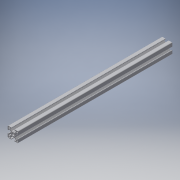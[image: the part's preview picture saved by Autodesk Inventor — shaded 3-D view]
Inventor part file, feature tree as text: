
AUTODESK INVENTOR PART (.ipt)
format: ipt  version: 2016 (Build 200138000, 138)  size: 312,832 bytes
history: native  units: in
note: dims shown in document units (in); Inventor stores cm internally (conversion verified against a paired STEP export)
features: other x3, extrude x1, sketch x1
ambient origin geometry x8: Origin, YZ Plane, XZ Plane, XY Plane, X Axis, Y Axis, Z Axis, Center Point
bodies: Solid1 (feature_tree)
feature tree (5):
  other  "Blocks"
  extrude  "Extrusion1"  [1 undecoded]
  sketch  "Sketch1"  dims[d1=0.0in]
  other  "Bosch 30x30 profile"
  other  "Bosch 30x30 profile:1"
note: 1 required parameter value undecoded (feature->parameter linkage not recoverable at this tier; creation-order binding heuristic only, values carry confidence <= 0.55)
